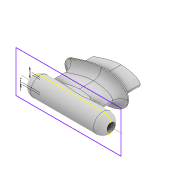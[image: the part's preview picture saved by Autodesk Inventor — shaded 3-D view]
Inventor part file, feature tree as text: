
AUTODESK INVENTOR PART (.ipt)
format: ipt  version: 2022 (Build 260153000, 153)  size: 439,808 bytes
history: native  units: mm
features: projected_geometry x10, extrude x9, sketch x9, fillet x3, plane x2, loft x1, other x1, revolve x1, chamfer x1
ambient origin geometry x8: Origin, YZ Plane, XZ Plane, XY Plane, X Axis, Y Axis, Z Axis, Center Point
bodies: Solid1 (feature_tree)
feature tree (37):
  extrude  "Extrusion1"  Depth=8.0mm
  extrude  "Extrusion2"  Depth=4.0mm
  plane  "Work Plane1"
  sketch  "Sketch3"  dims[d4=3.0mm d5=3.0mm d6=0.0mm d7=4.0mm]
  sketch  "Sketch5"  dims[d8=2.0mm d9=26.0mm]
  loft  "Loft2"
  fillet  "Fillet1"  [1 undecoded]
  fillet  "Fillet2"  Radius=4.0mm
  extrude  "Extrusion3"  Depth=26.0mm
  sketch  "Sketch7"  dims[d12=1.0mm d13=0.0mm]
  other  "Work Axis1"
  revolve  "Revolution1"  [1 undecoded]
  extrude  "Extrusion4"  TaperAngle=0.0deg  [1 undecoded]
  plane  "Work Plane3"
  extrude  "Extrusion5"  Depth=10.0mm
  fillet  "Fillet3"  Radius=5.0mm
  sketch  "Sketch10"  dims[d26=4.5mm d27=10.0mm d28=5.0mm d29=10.0mm d30=0.0mm d31=90.0deg d32=0.0mm d33=90.0deg d34=4.5mm d35=1.0mm d36=14.0mm d37=0.0mm d38=1.0mm d39=1.0mm d40=1.0mm d41=1.0mm d42=1.0mm d43=1.0mm d44=1.0mm d45=1.0mm d62=4.0mm d63=360.0deg d64=4.2mm d65=10.0mm d66=0.0mm d67=8.0mm d68=-16.5mm d69=4.0mm d70=4.0mm d71=4.0mm d72=4.0mm d73=4.0mm d74=0.5mm d75=0.0mm d76=4.0mm d77=1.0mm d78=1.0mm d79=17.5mm d80=0.0mm d81=1.4mm d82=0.0mm d85=0.0mm d86=0.0mm d87=1.2mm d88=0.0mm d89=0.4mm d90=2.0mm d91=45.0deg]
  extrude  "Unsuppress for Bottom Half (1/2)"  Depth=10.0mm
  extrude  "Unsuppress for Bottom Half (2/2)"  Depth=5.0mm
  extrude  "Unsuppress for Top Half (1/3)"  Depth=10.0mm
  extrude  "Unsuppress for Top Half (2/3)"  TaperAngle=0.0deg  [1 undecoded]
  chamfer  "Unsuppress for Top Half (3/3)"  Angle=90.0deg  [1 undecoded]
  sketch  "Sketch1"  dims[d0=4.0mm d1=8.0mm]
  sketch  "Sketch2"  dims[d2=4.0mm d3=4.0mm]
  projected_geometry  "Projected Loop1"
  sketch  "Sketch6"  dims[d10=26.0mm d11=5.0mm]
  projected_geometry  "Projected Loop4"
  projected_geometry  "Projected Loop5"
  projected_geometry  "Projected Loop6"
  projected_geometry  "Projected Loop7"
  sketch  "Sketch8"  dims[d14=22.0mm d15=0.0mm d16=10.0mm]
  sketch  "Sketch9"  dims[d17=14.0mm d18=28.0mm d19=0.0mm d20=0.0mm d21=5.0mm]
  projected_geometry  "Projected Loop8"
  projected_geometry  "Projected Loop9"
  projected_geometry  "Projected Loop10"
  projected_geometry  "Projected Loop11"
  projected_geometry  "Projected Loop12"
note: 5 required parameter values undecoded (feature->parameter linkage not recoverable at this tier; creation-order binding heuristic only, values carry confidence <= 0.55)